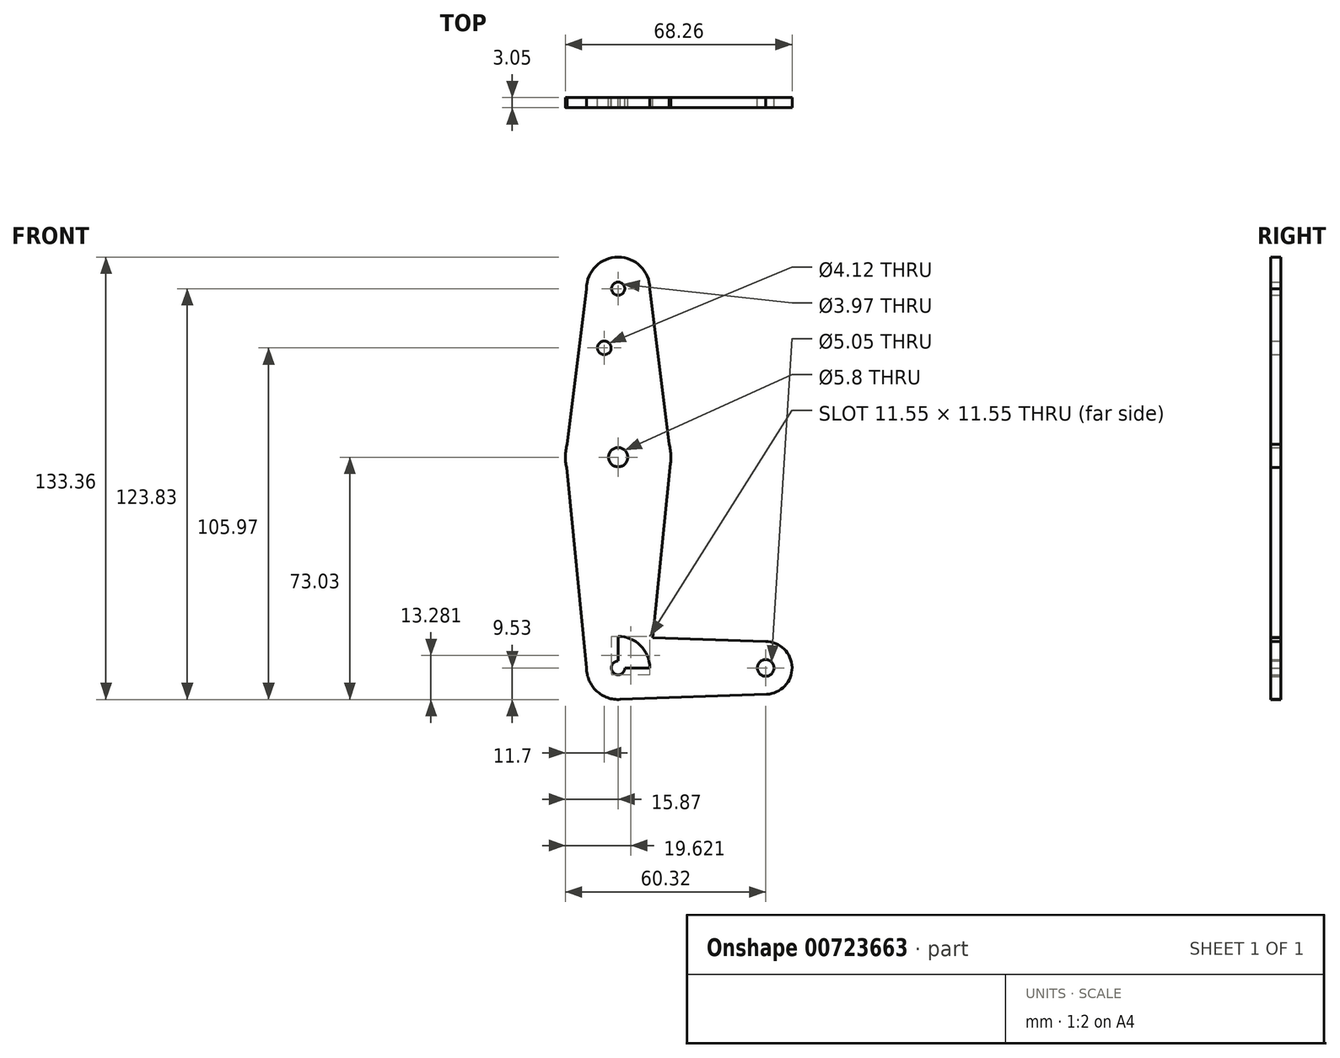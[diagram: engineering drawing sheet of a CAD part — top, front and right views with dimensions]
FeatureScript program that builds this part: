
annotation { "Feature Type Name" : "Feature", "Feature Type Description" : "" }
export const myFeature = defineFeature(function(context is Context, id is Id, definition is map)
    precondition{}
    {
        {
            var Q0;
            Q0=qCreatedBy(makeId("Front.planeOp"),FACE);
            var sketch = newSketch(context, id + "F0", { "sketchPlane" : qUnion([Q0])});
            skLineSegment(sketch, "E0", {"start": v(0, 114.3) * mm, "end": v(0, 0) * mm});
            skLineSegment(sketch, "E1", {"start": v(0, 0) * mm, "end": v(44.45, 0) * mm});
            skCircle(sketch, "E2", {"center": v(0, 114.3) * mm, "radius": 9.53 * mm});
            skCircle(sketch, "E3", {"center": v(0, 63.5) * mm, "radius": 15.88 * mm});
            skCircle(sketch, "E4", {"center": v(0, 0) * mm, "radius": 9.53 * mm});
            skCircle(sketch, "E5", {"center": v(44.45, 0) * mm, "radius": 7.94 * mm});
            skLineSegment(sketch, "E6", {"start": v(-9.53, 114.3) * mm, "end": v(-15.87, 63.5) * mm});
            skLineSegment(sketch, "E7", {"start": v(9.52, 114.3) * mm, "end": v(15.88, 63.5) * mm});
            skLineSegment(sketch, "E8", {"start": v(-15.87, 63.5) * mm, "end": v(-9.52, 0) * mm});
            skLineSegment(sketch, "E9", {"start": v(15.88, 63.5) * mm, "end": v(9.52, 0) * mm});
            skLineSegment(sketch, "E10", {"start": v(44.45, 7.94) * mm, "end": v(0, 9.52) * mm});
            skLineSegment(sketch, "E11", {"start": v(0, -9.53) * mm, "end": v(44.73, -7.93) * mm});
            skCircle(sketch, "E12", {"center": v(0, 0) * mm, "radius": 2.06 * mm});
            skCircle(sketch, "E13", {"center": v(0, 63.5) * mm, "radius": 2.9 * mm});
            skCircle(sketch, "E14", {"center": v(44.45, 0) * mm, "radius": 2.52 * mm});
            skCircle(sketch, "E15", {"center": v(-4.17, 96.44) * mm, "radius": 2.06 * mm});
            skCircle(sketch, "E16", {"center": v(0, 114.3) * mm, "radius": 1.99 * mm});
            skSolve(sketch);
        }
        {
            var Q0;
            Q0 = qSketchRegion(id + "F0", true);
            extrude(context, id + "F1", {"entities" : qUnion([Q0]), "depth" : 3.05 * mm, "offsetDistance" : 25.4 * mm});
        }
    });
